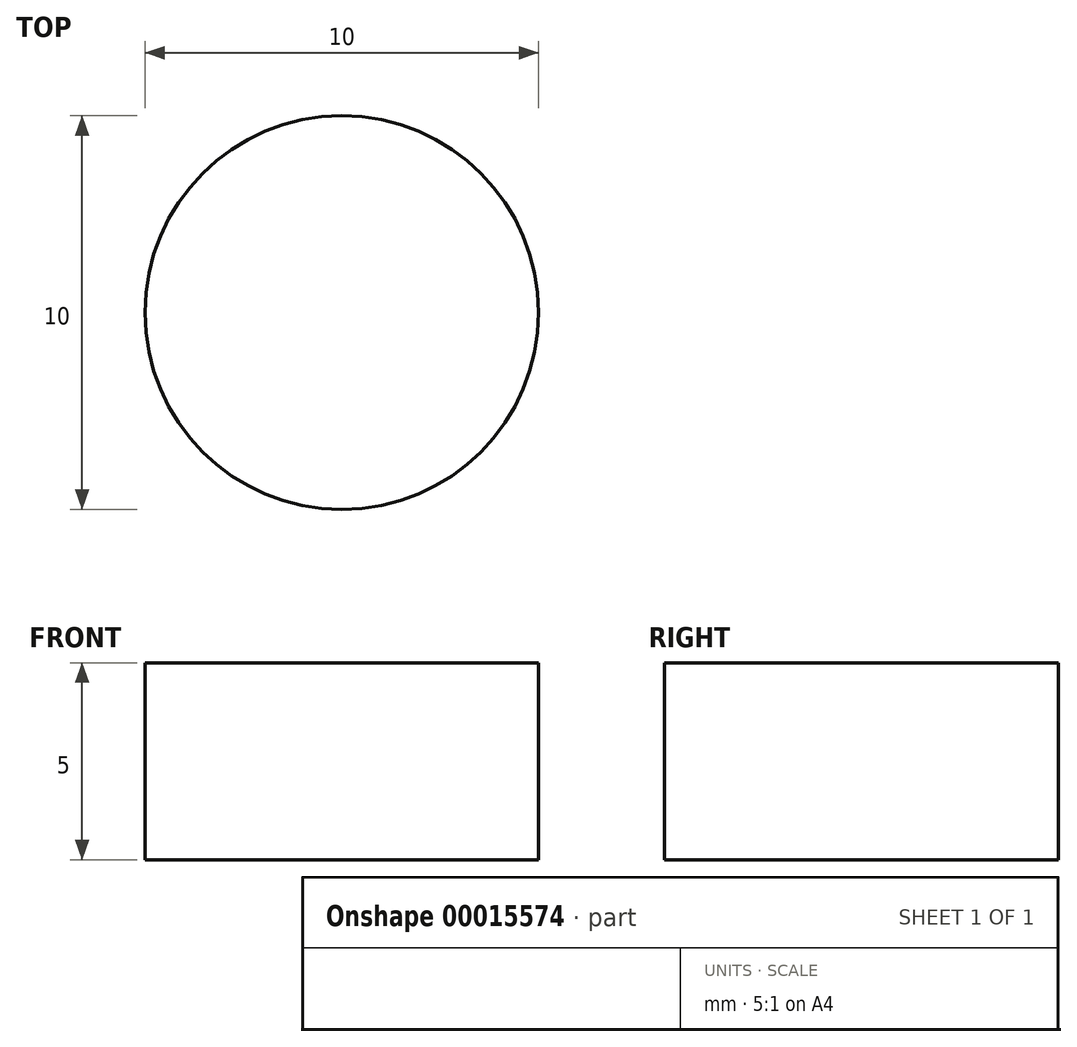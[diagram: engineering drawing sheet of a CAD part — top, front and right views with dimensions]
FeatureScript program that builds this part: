
annotation { "Feature Type Name" : "Feature", "Feature Type Description" : "" }
export const myFeature = defineFeature(function(context is Context, id is Id, definition is map)
    precondition{}
    {
        {
            var Q0;
            Q0=qCreatedBy(makeId("Top.planeOp"),FACE);
            var sketch = newSketch(context, id + "F0", { "sketchPlane" : qUnion([Q0])});
            skCircle(sketch, "E0", {"center": v(0, 0) * mm, "radius": 5 * mm});
            skSolve(sketch);
        }
        {
            var Q0;
            Q0=qSketchRegion(id+"F0",true);
            extrude(context, id + "F1", {"entities" : qUnion([Q0]), "depth" : 5 * mm});
        }
    });
